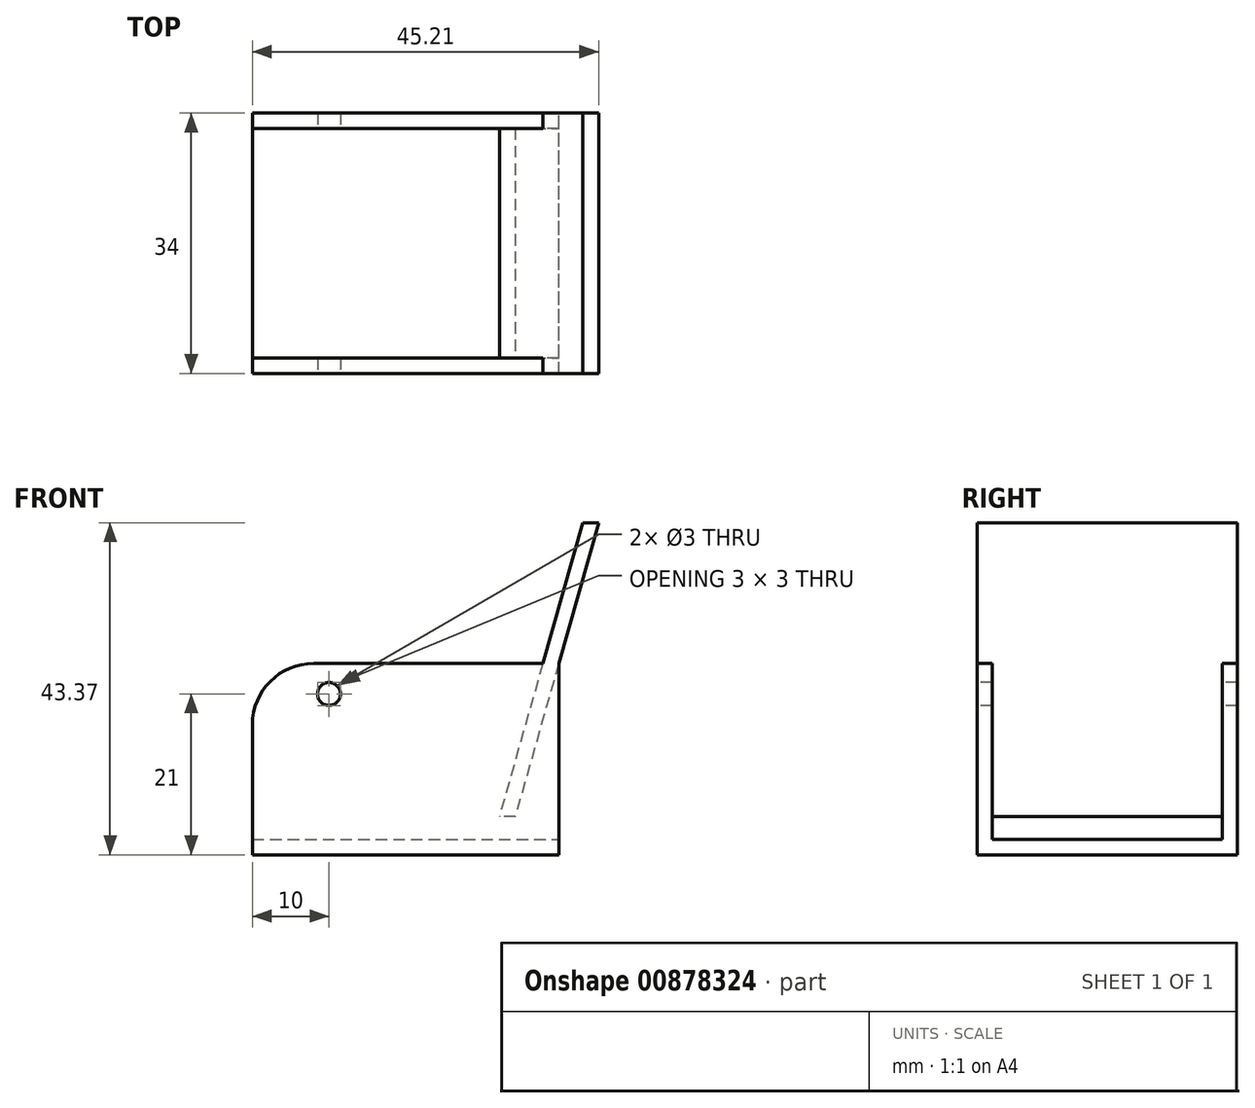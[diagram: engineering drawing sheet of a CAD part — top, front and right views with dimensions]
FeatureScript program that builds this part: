
annotation { "Feature Type Name" : "Feature", "Feature Type Description" : "" }
export const myFeature = defineFeature(function(context is Context, id is Id, definition is map)
    precondition{}
    {
        {
            var Q0;
            Q0=qCreatedBy(makeId("Top.planeOp"),FACE);
            var sketch = newSketch(context, id + "F0", { "sketchPlane" : qUnion([Q0])});
            skLineSegment(sketch, "E0.bottom", {"start": v(20, -17) * mm, "end": v(-20, -17) * mm});
            skLineSegment(sketch, "E0.top", {"start": v(20, 17) * mm, "end": v(-20, 17) * mm});
            skLineSegment(sketch, "E0.left", {"start": v(20, -17) * mm, "end": v(20, 17) * mm});
            skLineSegment(sketch, "E0.right", {"start": v(-20, -17) * mm, "end": v(-20, 17) * mm});
            skPoint(sketch, "E0.middle", {"position": v(0, 0) * mm});
            skLineSegment(sketch, "E1", {"start": v(-20, -15) * mm, "end": v(0, -15) * mm});
            skLineSegment(sketch, "E2", {"start": v(-20, 15) * mm, "end": v(0, 15) * mm});
            skLineSegment(sketch, "E3", {"start": v(0, 15) * mm, "end": v(20, 15) * mm});
            skLineSegment(sketch, "E4", {"start": v(0, -15) * mm, "end": v(20, -15) * mm});
            skSolve(sketch);
        }
        {
            var Q0;
            {var subQ1=sQuery(id+"F0.wireOp",EDGE,"E1");Q0=makeQuery(id+"F0.imprint","IMPRINT",FACE,{"disambiguationData":[TD([[makeQuery(id+"F0.imprint","IMPRINT",EDGE,{"derivedFrom":subQ1}),1.0]])]});}
            extrude(context, id + "F1", {"entities" : qUnion([Q0]), "depth" : 2 * mm, "offsetDistance" : 25 * mm});
        }
        {
            var Q0;
            {var subQ1=sQuery(id+"F0.wireOp",EDGE,"E0.top");Q0=makeQuery(id+"F0.imprint","IMPRINT",FACE,{"disambiguationData":[TD([[makeQuery(id+"F0.imprint","IMPRINT",EDGE,{"derivedFrom":subQ1}),1.0]])]});}
            var Q1;
            {var subQ2=sQuery(id+"F0.wireOp",EDGE,"E0.bottom");Q1=makeQuery(id+"F0.imprint","IMPRINT",FACE,{"disambiguationData":[TD([[makeQuery(id+"F0.imprint","IMPRINT",EDGE,{"derivedFrom":subQ2}),-1.0]])]});}
            extrude(context, id + "F2", {"entities" : qUnion([Q0, Q1]), "operationType" : NewBodyOperationType.ADD, "depth" : 25 * mm, "offsetDistance" : 25 * mm});
        }
        {
            var Q0;
            Q0=makeQuery(id+"F2.opExtrude","SWEPT_FACE",FACE,{"disambiguationData":[OSD([sQuery(id+"F0.wireOp",EDGE,"E0.bottom")])]});
            var sketch = newSketch(context, id + "F3", { "sketchPlane" : qUnion([Q0])});
            skCircle(sketch, "E5", {"center": v(-10, 21) * mm, "radius": 1.5 * mm});
            skLineSegment(sketch, "E6.bottom", {"start": v(-12, 25) * mm, "end": v(20, 25) * mm});
            skLineSegment(sketch, "E6.top", {"start": v(-20, 0) * mm, "end": v(20, 0) * mm});
            skLineSegment(sketch, "E6.left", {"start": v(-20, 17) * mm, "end": v(-20, 0) * mm});
            skLineSegment(sketch, "E6.right", {"start": v(20, 25) * mm, "end": v(20, 0) * mm});
            skPoint(sketch, "E7.visualSharp", {"position": v(-20, 25) * mm});
            skArc(sketch, "E7.filletArc", {"start": v(-12, 25) * mm, "mid": v(-17.66, 22.66) * mm, "end": v(-20, 17) * mm});
            skLineSegment(sketch, "E8", {"start": v(-20, 2) * mm, "end": v(20, 2) * mm});
            skLineSegment(sketch, "E9", {"start": v(11.4, 2) * mm, "end": v(23.13, 43.37) * mm});
            skLineSegment(sketch, "E10", {"start": v(13.47, 2) * mm, "end": v(25.21, 43.37) * mm});
            skLineSegment(sketch, "E11", {"start": v(23.13, 43.37) * mm, "end": v(25.21, 43.37) * mm});
            skLineSegment(sketch, "E12", {"start": v(12.24, 5) * mm, "end": v(14.32, 5) * mm});
            skSolve(sketch);
        }
        {
            var Q0;
            {var subQ0=sQuery(id+"F3.wireOp",EDGE,"E7.filletArc");Q0=makeQuery(id+"F3.imprint","IMPRINT",FACE,{"disambiguationData":[TD([[makeQuery(id+"F3.imprint","IMPRINT",EDGE,{"derivedFrom":subQ0}),-1.0]])]});}
            var Q1;
            Q1=makeQuery(id+"F3.imprint","IMPRINT",FACE,{"disambiguationData":[TD([[makeQuery(id+"F3.imprint","IMPRINT",EDGE,{"derivedFrom":sQuery(id+"F3.wireOp",EDGE,"E5")}),1.0]])]});
            extrude(context, id + "F4", {"entities" : qUnion([Q0, Q1]), "operationType" : NewBodyOperationType.REMOVE, "oppositeDirection" : true, "depth" : 34 * mm, "offsetDistance" : 25 * mm});
        }
        {
            var Q0;
            {var subQ5=sQuery(id+"F3.wireOp",EDGE,"E12");Q0=makeQuery(id+"F3.imprint","IMPRINT",FACE,{"disambiguationData":[TD([[makeQuery(id+"F3.imprint","IMPRINT",EDGE,{"derivedFrom":subQ5}),1.0]])]});}
            var Q1;
            {var subQ5=sQuery(id+"F3.wireOp",EDGE,"E11");Q1=makeQuery(id+"F3.imprint","IMPRINT",FACE,{"disambiguationData":[TD([[makeQuery(id+"F3.imprint","IMPRINT",EDGE,{"derivedFrom":subQ5}),-1.0]])]});}
            extrude(context, id + "F5", {"entities" : qUnion([Q0, Q1]), "operationType" : NewBodyOperationType.ADD, "oppositeDirection" : true, "depth" : 34 * mm, "offsetDistance" : 25 * mm});
        }
    });
